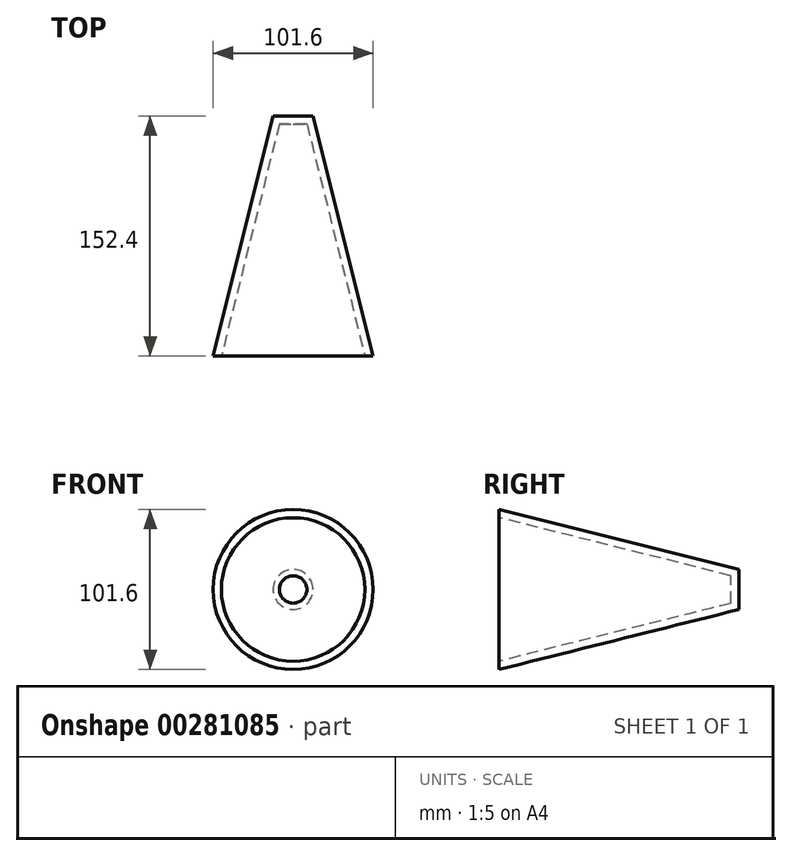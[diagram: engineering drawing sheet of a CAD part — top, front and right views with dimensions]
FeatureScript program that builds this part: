
annotation { "Feature Type Name" : "Feature", "Feature Type Description" : "" }
export const myFeature = defineFeature(function(context is Context, id is Id, definition is map)
    precondition{}
    {
        {
            var Q0;
            Q0=qCreatedBy(makeId("Front.planeOp"),FACE);
            cPlane(context, id + "F0", {"entities" : qUnion([Q0]), "cplaneType" : CPlaneType.OFFSET, "offset" : 152.4 * mm, "width" : 152.4 * mm, "height" : 152.4 * mm});
        }
        {
            var Q0;
            Q0=qCreatedBy(id+"F0.planeOp",FACE);
            var sketch = newSketch(context, id + "F1", { "sketchPlane" : qUnion([Q0])});
            skCircle(sketch, "E0", {"center": v(0, 0) * mm, "radius": 50.8 * mm});
            skSolve(sketch);
        }
        {
            var Q0;
            Q0=qCreatedBy(makeId("Front.planeOp"),FACE);
            var sketch = newSketch(context, id + "F2", { "sketchPlane" : qUnion([Q0])});
            skCircle(sketch, "E1", {"center": v(0, 0) * mm, "radius": 12.7 * mm});
            skSolve(sketch);
        }
        {
            var Q0;
            Q0=makeQuery(id+"F1.imprint","IMPRINT",FACE,{"disambiguationData":[TD([[makeQuery(id+"F1.imprint","IMPRINT",EDGE,{"derivedFrom":sQuery(id+"F1.wireOp",EDGE,"E0")}),1.0]])]});
            var Q1;
            Q1=makeQuery(id+"F2.imprint","IMPRINT",FACE,{"disambiguationData":[TD([[makeQuery(id+"F2.imprint","IMPRINT",EDGE,{"derivedFrom":sQuery(id+"F2.wireOp",EDGE,"E1")}),1.0]])]});
            loft(context, id + "F3", {"sheetProfilesArray" : [{ "sheetProfileEntities" : qUnion([Q0]) }, { "sheetProfileEntities" : qUnion([Q1]) }]});
        }
        {
            var Q0;
            Q0=makeQuery(id+"F3.opLoft","CAP_FACE",FACE,{"disambiguationData":[OSD([makeQuery(id+"F1.imprint","IMPRINT",FACE,{"disambiguationData":[TD([[makeQuery(id+"F1.imprint","IMPRINT",EDGE,{"derivedFrom":sQuery(id+"F1.wireOp",EDGE,"E0")}),1.0]])]})])],"isStart":true});
            shell(context, id + "F4", {"entities" : qUnion([Q0]), "thickness" : 5.08 * mm});
        }
    });
